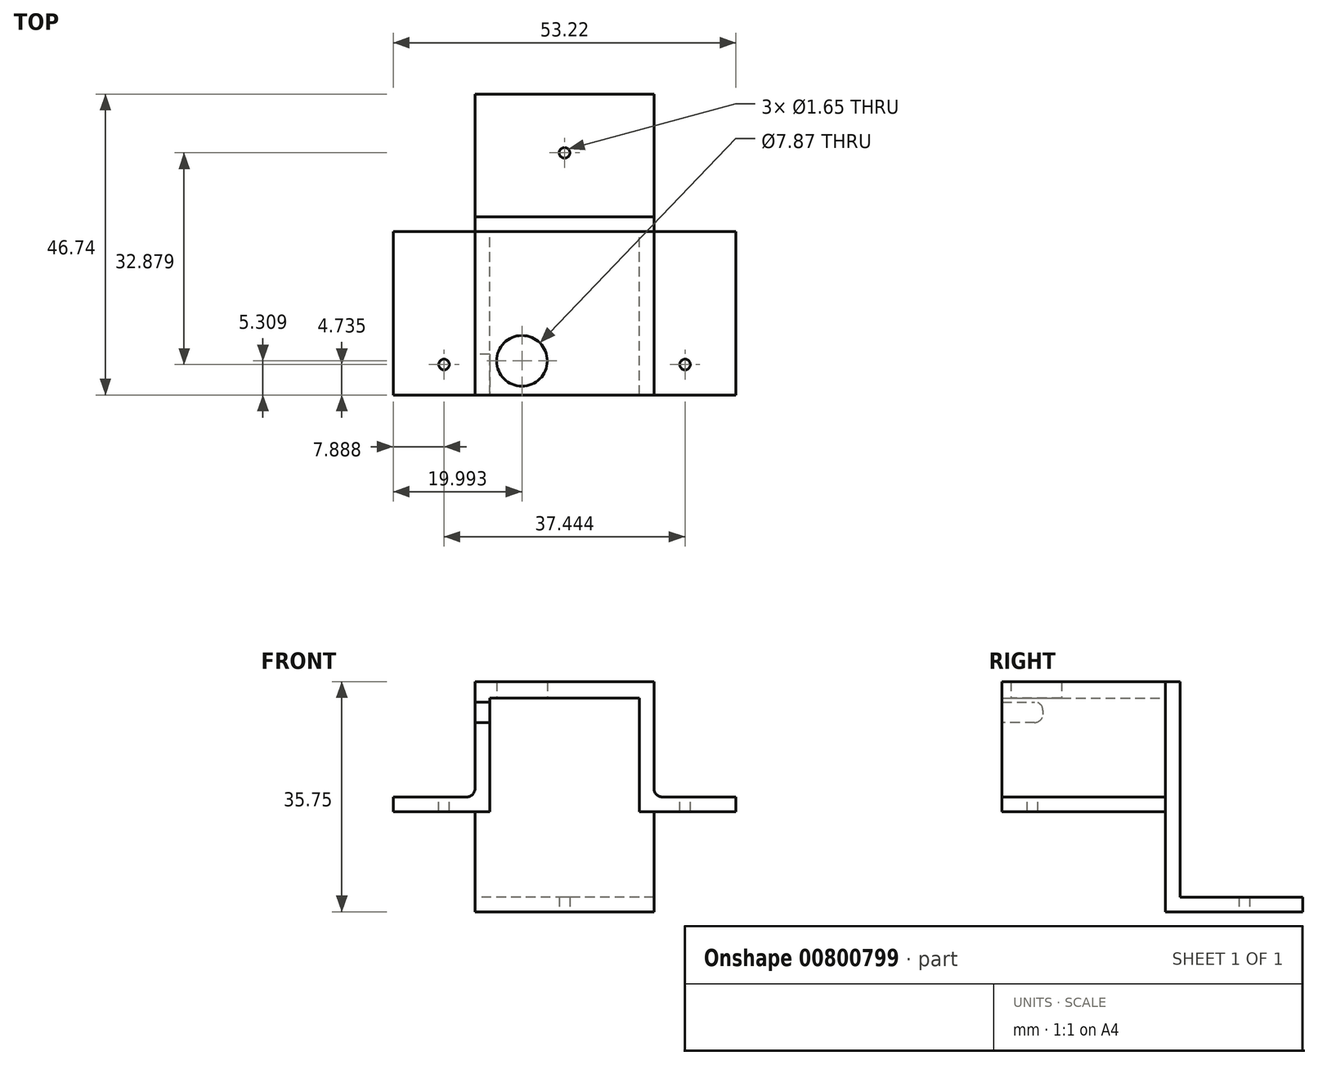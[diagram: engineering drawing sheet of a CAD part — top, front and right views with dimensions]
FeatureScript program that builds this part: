
annotation { "Feature Type Name" : "Feature", "Feature Type Description" : "" }
export const myFeature = defineFeature(function(context is Context, id is Id, definition is map)
    precondition{}
    {
        {
            var Q0;
            Q0=qCreatedBy(makeId("Front.planeOp"),FACE);
            var sketch = newSketch(context, id + "F0", { "sketchPlane" : qUnion([Q0])});
            skLineSegment(sketch, "E0.bottom", {"start": v(13.9, 10.1) * mm, "end": v(-13.9, 10.1) * mm});
            skLineSegment(sketch, "E0.left", {"start": v(13.9, 10.1) * mm, "end": v(13.9, -10.1) * mm});
            skLineSegment(sketch, "E0.right", {"start": v(-13.9, 10.1) * mm, "end": v(-13.9, -10.1) * mm});
            skPoint(sketch, "E0.middle", {"position": v(0, 0) * mm});
            skLineSegment(sketch, "E1.bottom", {"start": v(11.62, 7.56) * mm, "end": v(-11.62, 7.56) * mm});
            skLineSegment(sketch, "E1.left", {"start": v(11.62, 7.56) * mm, "end": v(11.62, -10.1) * mm});
            skLineSegment(sketch, "E1.right", {"start": v(-11.62, 7.56) * mm, "end": v(-11.62, -10.1) * mm});
            skLineSegment(sketch, "E2", {"start": v(11.62, -10.1) * mm, "end": v(13.9, -10.1) * mm});
            skLineSegment(sketch, "E3", {"start": v(-13.9, -10.1) * mm, "end": v(-11.62, -10.1) * mm});
            skLineSegment(sketch, "E4.bottom", {"start": v(13.9, -10.1) * mm, "end": v(26.6, -10.1) * mm});
            skLineSegment(sketch, "E4.top", {"start": v(13.9, -7.81) * mm, "end": v(26.6, -7.81) * mm});
            skLineSegment(sketch, "E4.left", {"start": v(13.9, -10.1) * mm, "end": v(13.9, -7.81) * mm});
            skLineSegment(sketch, "E4.right", {"start": v(26.6, -10.1) * mm, "end": v(26.6, -7.81) * mm});
            skLineSegment(sketch, "E5.bottom", {"start": v(-13.9, -10.1) * mm, "end": v(-26.6, -10.1) * mm});
            skLineSegment(sketch, "E5.top", {"start": v(-13.9, -7.81) * mm, "end": v(-26.6, -7.81) * mm});
            skLineSegment(sketch, "E5.left", {"start": v(-13.9, -10.1) * mm, "end": v(-13.9, -7.81) * mm});
            skLineSegment(sketch, "E5.right", {"start": v(-26.6, -10.1) * mm, "end": v(-26.6, -7.81) * mm});
            skSolve(sketch);
        }
        {
            var Q0;
            Q0=makeQuery(id+"F0.imprint","IMPRINT",FACE,{"disambiguationData":[TD([[makeQuery(id+"F0.imprint","IMPRINT",EDGE,{"derivedFrom":sQuery(id+"F0.wireOp",EDGE,"E0.bottom")}),1.0]])]});
            var Q1;
            Q1=makeQuery(id+"F0.imprint","IMPRINT",FACE,{"disambiguationData":[TD([[makeQuery(id+"F0.imprint","IMPRINT",EDGE,{"derivedFrom":sQuery(id+"F0.wireOp",EDGE,"E5.bottom")}),-1.0]])]});
            var Q2;
            Q2=makeQuery(id+"F0.imprint","IMPRINT",FACE,{"disambiguationData":[TD([[makeQuery(id+"F0.imprint","IMPRINT",EDGE,{"derivedFrom":sQuery(id+"F0.wireOp",EDGE,"E4.bottom")}),1.0]])]});
            extrude(context, id + "F1", {"entities" : qUnion([Q0, Q1, Q2]), "endBound" : BoundingType.SYMMETRIC, "depth" : 25.4 * mm, "offsetDistance" : 25.4 * mm});
        }
        {
            var Q0;
            Q0=qCreatedBy(makeId("Right.planeOp"),FACE);
            var sketch = newSketch(context, id + "F2", { "sketchPlane" : qUnion([Q0])});
            skLineSegment(sketch, "E6.bottom", {"start": v(12.7, 10.08) * mm, "end": v(14.99, 10.08) * mm});
            skLineSegment(sketch, "E6.top", {"start": v(12.7, -25.65) * mm, "end": v(14.99, -25.65) * mm});
            skLineSegment(sketch, "E6.left", {"start": v(12.7, 10.08) * mm, "end": v(12.7, -25.65) * mm});
            skLineSegment(sketch, "E6.right", {"start": v(14.99, 10.08) * mm, "end": v(14.99, -25.65) * mm});
            skLineSegment(sketch, "E7.bottom", {"start": v(14.99, -25.65) * mm, "end": v(34.04, -25.65) * mm});
            skLineSegment(sketch, "E7.top", {"start": v(14.99, -23.37) * mm, "end": v(34.04, -23.37) * mm});
            skLineSegment(sketch, "E7.left", {"start": v(14.99, -25.65) * mm, "end": v(14.99, -23.37) * mm});
            skLineSegment(sketch, "E7.right", {"start": v(34.04, -25.65) * mm, "end": v(34.04, -23.37) * mm});
            skSolve(sketch);
        }
        {
            var Q0;
            Q0 = qSketchRegion(id + "F2", true);
            extrude(context, id + "F3", {"entities" : qUnion([Q0]), "endBound" : BoundingType.SYMMETRIC, "depth" : 27.8 * mm, "offsetDistance" : 25.4 * mm});
        }
        {
            var Q0;
            Q0=makeQuery(id+"F1.opExtrude","SWEPT_FACE",FACE,{"disambiguationData":[OSD([sQuery(id+"F0.wireOp",EDGE,"E3"),sQuery(id+"F0.wireOp",EDGE,"E5.bottom")])]});
            var sketch = newSketch(context, id + "F4", { "sketchPlane" : qUnion([Q0])});
            skCircle(sketch, "E8", {"center": v(-18.72, 7.96) * mm, "radius": 0.83 * mm});
            skCircle(sketch, "E9.MirrorC", {"center": v(18.72, 7.96) * mm, "radius": 0.83 * mm});
            skSolve(sketch);
        }
        {
            var Q0;
            Q0=makeQuery(id+"F1.opExtrude","SWEPT_FACE",FACE,{"disambiguationData":[OSD([sQuery(id+"F0.wireOp",EDGE,"E0.bottom")])]});
            var sketch = newSketch(context, id + "F5", { "sketchPlane" : qUnion([Q0])});
            skCircle(sketch, "E10", {"center": v(-6.62, -7.4) * mm, "radius": 3.94 * mm});
            skCircle(sketch, "E11", {"center": v(0, 24.91) * mm, "radius": 0.83 * mm});
            skSolve(sketch);
        }
        {
            var Q0;
            Q0 = qSketchRegion(id + "F5", true);
            extrude(context, id + "F6", {"entities" : qUnion([Q0]), "operationType" : NewBodyOperationType.REMOVE, "endBound" : BoundingType.SYMMETRIC, "depth" : 127 * mm, "offsetDistance" : 25.4 * mm});
        }
        {
            var Q0;
            Q0 = qSketchRegion(id + "F4", true);
            extrude(context, id + "F7", {"entities" : qUnion([Q0]), "operationType" : NewBodyOperationType.REMOVE, "endBound" : BoundingType.SYMMETRIC, "depth" : 127 * mm, "offsetDistance" : 25.4 * mm});
        }
        {
            var Q0;
            Q0=makeQuery(id+"F1.opExtrude","SWEPT_FACE",FACE,{"disambiguationData":[OSD([sQuery(id+"F0.wireOp",EDGE,"E0.right")])]});
            var sketch = newSketch(context, id + "F8", { "sketchPlane" : qUnion([Q0])});
            skLineSegment(sketch, "E12", {"start": v(12.7, 6.92) * mm, "end": v(6.35, 6.92) * mm});
            skLineSegment(sketch, "E13", {"start": v(6.35, 6.92) * mm, "end": v(6.35, 3.75) * mm});
            skLineSegment(sketch, "E14", {"start": v(6.35, 3.75) * mm, "end": v(12.7, 3.75) * mm});
            skSolve(sketch);
        }
        {
            var Q0;
            {var subQ0=sQuery(id+"F8.wireOp",EDGE,"E12");Q0=makeQuery(id+"F8.imprint","IMPRINT",FACE,{"disambiguationData":[TD([[makeQuery(id+"F8.imprint","IMPRINT",EDGE,{"derivedFrom":subQ0}),1.0]])]});}
            extrude(context, id + "F9", {"entities" : qUnion([Q0]), "operationType" : NewBodyOperationType.REMOVE, "oppositeDirection" : true, "depth" : 25.4 * mm, "offsetDistance" : 25.4 * mm});
        }
        {
            var Q0;
            Q0=makeQuery(id+"F9.boolean.opBoolean","COPY",EDGE,{"derivedFrom":makeQuery(id+"F9.opExtrude","SWEPT_EDGE",EDGE,{"disambiguationData":[OSD([sQuery(id+"F8.wireOp",EDGE,"E13"),sQuery(id+"F8.wireOp",EDGE,"E14")])]})});
            var Q1;
            Q1=makeQuery(id+"F9.boolean.opBoolean","COPY",EDGE,{"derivedFrom":makeQuery(id+"F9.opExtrude","SWEPT_EDGE",EDGE,{"disambiguationData":[OSD([sQuery(id+"F8.wireOp",EDGE,"E12"),sQuery(id+"F8.wireOp",EDGE,"E13")])]})});
            var Q2;
            Q2=makeQuery(id+"F1.opExtrude","SWEPT_EDGE",EDGE,{"disambiguationData":[OSD([sQuery(id+"F0.wireOp",EDGE,"E0.right"),sQuery(id+"F0.wireOp",EDGE,"E5.top"),sQuery(id+"F0.wireOp",EDGE,"E5.left")])]});
            var Q3;
            Q3=makeQuery(id+"F1.opExtrude","SWEPT_EDGE",EDGE,{"disambiguationData":[OSD([sQuery(id+"F0.wireOp",EDGE,"E0.left"),sQuery(id+"F0.wireOp",EDGE,"E4.top"),sQuery(id+"F0.wireOp",EDGE,"E4.left")])]});
            fillet(context, id + "F10", {"entities" : qUnion([Q0, Q1, Q2, Q3]), "radius" : 1.27 * mm, "tangentPropagation" : true, "allowEdgeOverflow" : false});
        }
    });
